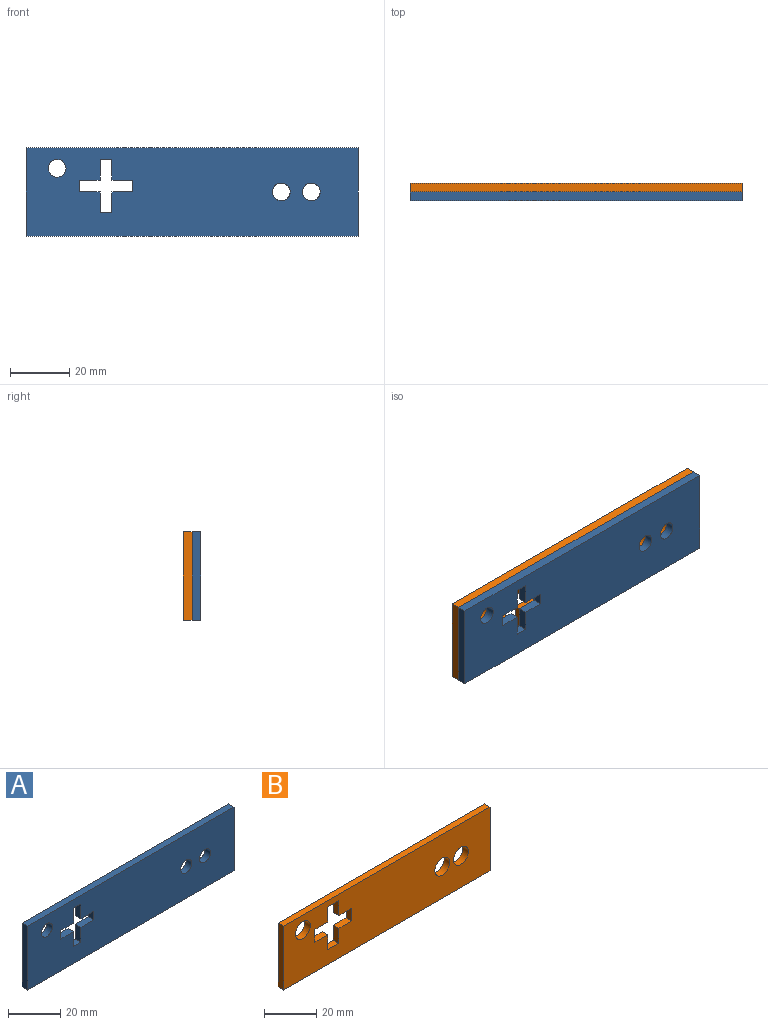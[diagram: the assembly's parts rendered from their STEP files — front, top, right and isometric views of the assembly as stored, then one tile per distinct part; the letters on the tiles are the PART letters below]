
ASSEMBLY  parts=2 mates=1
PART A: 21 faces, bbox 112x3x30 mm
  f0: plane 112x30mm, normal (0,-1,0), area 3147.2mm2, adj f2,f3,f4,f5,f6,f7,f8,f9
  f1: plane 112x30mm, normal (0,1,0), area 3147.2mm2, adj f2,f3,f4,f5,f6,f7,f8,f9
  f2: plane 112x3mm, normal (0,0,-1), area 336mm2, adj f0,f1,f3,f6
  f3: plane 30x3mm, normal (1,0,0), area 90mm2, adj f0,f1,f2,f4
  f4: plane 112x3mm, normal (0,0,1), area 336mm2, adj f0,f1,f3,f6
  f5: cylinder r=3mm len=6mm, axis (0,1,0), area 56.5mm2, adj f0,f1
  f6: plane 30x3mm, normal (-1,0,0), area 90mm2, adj f0,f1,f2,f4
  f7: plane 4x3mm, normal (-1,0,0), area 12mm2, adj f0,f1,f8,f18
  f8: plane 7x3mm, normal (0,0,-1), area 21mm2, adj f0,f1,f7,f9
  f9: plane 7x3mm, normal (-1,0,0), area 21mm2, adj f0,f1,f8,f10
  f10: plane 4x3mm, normal (0,0,-1), area 12mm2, adj f0,f1,f9,f11
  f11: plane 7x3mm, normal (1,0,0), area 21mm2, adj f0,f1,f10,f12
  f12: plane 7x3mm, normal (0,0,-1), area 21mm2, adj f0,f1,f11,f13
  f13: plane 4x3mm, normal (1,0,0), area 12mm2, adj f0,f1,f12,f14
  f14: plane 7x3mm, normal (0,0,1), area 21mm2, adj f0,f1,f13,f15
  f15: plane 7x3mm, normal (1,0,0), area 21mm2, adj f0,f1,f14,f16
  f16: plane 4x3mm, normal (0,0,1), area 12mm2, adj f0,f1,f15,f17
  f17: plane 7x3mm, normal (-1,0,0), area 21mm2, adj f0,f1,f16,f18
  f18: plane 7x3mm, normal (0,0,1), area 21mm2, adj f0,f1,f7,f17
  f19: cylinder r=3mm len=6mm, axis (0,-1,0), area 56.5mm2, adj f0,f1
  f20: cylinder r=3mm len=6mm, axis (0,-1,0), area 56.5mm2, adj f0,f1
PART B: 21 faces, bbox 112x3x30 mm
  f0: plane 112x30mm, normal (0,-1,0), area 3005.2mm2, adj f2,f3,f4,f5,f6,f7,f8,f9
  f1: plane 112x30mm, normal (0,1,0), area 3005.2mm2, adj f2,f3,f4,f5,f6,f7,f8,f9
  f2: plane 112x3mm, normal (0,0,-1), area 336mm2, adj f0,f1,f3,f6
  f3: plane 30x3mm, normal (1,0,0), area 90mm2, adj f0,f1,f2,f4
  f4: plane 112x3mm, normal (0,0,1), area 336mm2, adj f0,f1,f3,f6
  f5: cylinder r=4mm len=8mm, axis (0,1,0), area 75.4mm2, adj f0,f1
  f6: plane 30x3mm, normal (-1,0,0), area 90mm2, adj f0,f1,f2,f4
  f7: plane 6x3mm, normal (-1,0,0), area 18mm2, adj f0,f1,f8,f18
  f8: plane 7x3mm, normal (0,0,-1), area 21mm2, adj f0,f1,f7,f9
  f9: plane 7x3mm, normal (-1,0,0), area 21mm2, adj f0,f1,f8,f10
  f10: plane 6x3mm, normal (0,0,-1), area 18mm2, adj f0,f1,f9,f11
  f11: plane 7x3mm, normal (1,0,0), area 21mm2, adj f0,f1,f10,f12
  f12: plane 7x3mm, normal (0,0,-1), area 21mm2, adj f0,f1,f11,f13
  f13: plane 6x3mm, normal (1,0,0), area 18mm2, adj f0,f1,f12,f14
  f14: plane 7x3mm, normal (0,0,1), area 21mm2, adj f0,f1,f13,f15
  f15: plane 7x3mm, normal (1,0,0), area 21mm2, adj f0,f1,f14,f16
  f16: plane 6x3mm, normal (0,0,1), area 18mm2, adj f0,f1,f15,f17
  f17: plane 7x3mm, normal (-1,0,0), area 21mm2, adj f0,f1,f16,f18
  f18: plane 7x3mm, normal (0,0,1), area 21mm2, adj f0,f1,f7,f17
  f19: cylinder r=4mm len=8mm, axis (0,-1,0), area 75.4mm2, adj f0,f1
  f20: cylinder r=4mm len=8mm, axis (0,-1,0), area 75.4mm2, adj f0,f1
PLACE A t=(-10.12,18.83,13.57)mm
PLACE B t=(-10.12,21.83,13.57)mm
MATE fastened A.f1 <-> B.f0  axis (0,1,0) through (-66.12,18.83,13.57)mm
